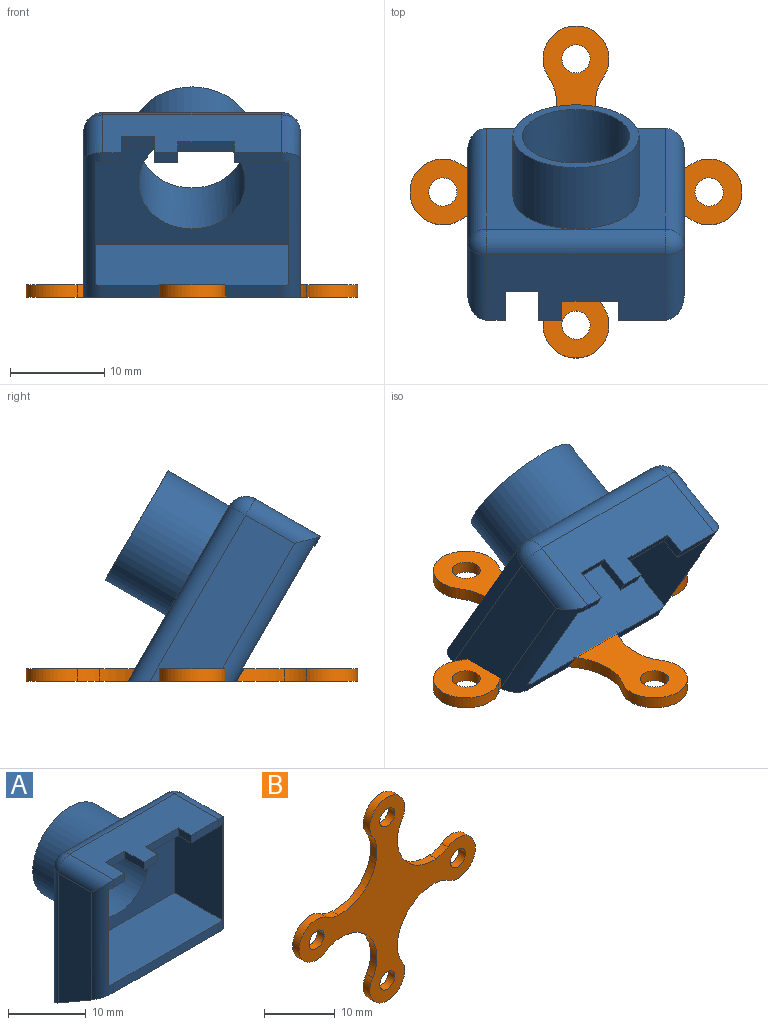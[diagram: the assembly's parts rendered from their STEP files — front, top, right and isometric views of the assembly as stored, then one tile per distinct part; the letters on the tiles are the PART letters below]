
ASSEMBLY  parts=2 mates=1
PART A: 32 faces, bbox 23x17.5x23.5 mm
  f0: plane 19x1.43mm, normal (0,-1,0), area 27.1mm2, adj f9,f22,f23,f29
  f1: plane 2x1.2mm, normal (0,-1,0), area 2.4mm2, adj f5,f6,f16,f23
  f2: plane 5x1.2mm, normal (0,-1,0), area 6mm2, adj f5,f6,f19,f29
  f3: plane 20.35x6mm, normal (1,0,0), area 111.7mm2, adj f22,f28,f29,f31
  f4: plane 2.5x1.2mm, normal (0,-1,0), area 3mm2, adj f5,f6,f17,f21
  f5: plane 19x8mm, normal (0,0,1), area 126mm2, adj f1,f2,f4,f16,f17,f18,f19,f20
  f6: plane 20.6x8.8mm, normal (0,0,-1), area 155.1mm2, adj f1,f2,f4,f10,f11,f12,f16,f17
  f7: plane 20.35x6mm, normal (-1,0,0), area 111.7mm2, adj f22,f23,f24,f25
  f8: plane 21.5x19mm, normal (0,1,0), area 267.5mm2, adj f14,f22,f25,f27,f28
  f9: plane 20.6x8.8mm, normal (0,0,1), area 181.2mm2, adj f0,f10,f11,f12,f23,f29
  f10: plane 15.1x8.63mm, normal (-1,0,0), area 130.4mm2, adj f6,f9,f12,f29
  f11: plane 15.1x8.63mm, normal (1,0,0), area 130.4mm2, adj f6,f9,f12,f23
  f12: plane 20.6x15.1mm, normal (0,-1,0), area 209mm2, adj f6,f9,f10,f11,f13
  f13: cylinder r=5.7mm len=11.4mm, axis (0,1,0), area 311.6mm2, adj f12,f15
  f14: cylinder r=6.7mm len=13.4mm, axis (0,-1,0), area 315.7mm2, adj f8,f15
  f15: plane 13.4x13.4mm, normal (0,1,0), area 39mm2, adj f13,f14
  f16: plane 3.5x1.2mm, normal (1,0,0), area 4.2mm2, adj f1,f5,f6,f18
  f17: plane 3.5x1.2mm, normal (-1,0,0), area 4.2mm2, adj f4,f5,f6,f18
  f18: plane 3.5x1.2mm, normal (0,-1,0), area 4.2mm2, adj f5,f6,f16,f17
  f19: plane 2.3x1.2mm, normal (-1,0,0), area 2.8mm2, adj f2,f5,f6,f20
  f20: plane 6x1.2mm, normal (0,-1,0), area 7.2mm2, adj f5,f6,f19,f21
  f21: plane 2.3x1.2mm, normal (1,0,0), area 2.8mm2, adj f4,f5,f6,f20
  f22: plane 23x10mm, normal (0,-0.5,-0.87), area 261.6mm2, adj f0,f3,f7,f8,f23,f25,f28,f29
  f23: cylinder r=2mm len=18.88mm, axis (0,0,1), area 42.3mm2, adj f0,f1,f6,f7,f9,f11,f22,f24
  f24: cylinder r=2mm len=8mm, axis (0,-1,0), area 22.8mm2, adj f5,f7,f23,f26
  f25: cylinder r=2mm len=21.5mm, axis (0,0,-1), area 66.2mm2, adj f7,f8,f22,f26
  f26: sphere r=2mm, area 6.3mm2, adj f24,f25,f27
  f27: cylinder r=2mm len=19mm, axis (-1,0,0), area 59.7mm2, adj f5,f8,f26,f30
  f28: cylinder r=2mm len=21.5mm, axis (0,0,1), area 66.2mm2, adj f3,f8,f22,f30
  f29: cylinder r=2mm len=18.88mm, axis (0,0,-1), area 42.3mm2, adj f0,f2,f3,f6,f9,f10,f22,f31
  f30: sphere r=2mm, area 6.3mm2, adj f27,f28,f31
  f31: cylinder r=2mm len=8mm, axis (0,1,0), area 22.8mm2, adj f3,f5,f29,f30
PART B: 22 faces, bbox 35.3x1.3x35.3 mm
  f0: cylinder r=5mm len=2.39mm, axis (0,1,0), area 3.3mm2, adj f1,f19,f20,f21
  f1: cylinder r=3.5mm len=7mm, axis (0,1,0), area 19.7mm2, adj f0,f2,f20,f21
  f2: cylinder r=5mm len=2.39mm, axis (0,1,0), area 3.3mm2, adj f1,f3,f20,f21
  f3: cylinder r=7.18mm len=7.75mm, axis (0,1,0), area 16.1mm2, adj f2,f4,f20,f21
  f4: cylinder r=5mm len=2.39mm, axis (0,1,0), area 3.3mm2, adj f3,f5,f20,f21
  f5: cylinder r=3.5mm len=7mm, axis (0,1,0), area 19.7mm2, adj f4,f6,f20,f21
  f6: cylinder r=5mm len=2.39mm, axis (0,1,0), area 3.3mm2, adj f5,f7,f20,f21
  f7: cylinder r=7.18mm len=7.75mm, axis (0,1,0), area 16.1mm2, adj f6,f8,f20,f21
  f8: cylinder r=5mm len=2.39mm, axis (0,1,0), area 3.3mm2, adj f7,f9,f20,f21
  f9: cylinder r=3.5mm len=7mm, axis (0,1,0), area 19.7mm2, adj f8,f10,f20,f21
  f10: cylinder r=5mm len=2.39mm, axis (0,1,0), area 3.3mm2, adj f9,f11,f20,f21
  f11: cylinder r=7.18mm len=7.75mm, axis (0,1,0), area 16.1mm2, adj f10,f12,f20,f21
  f12: cylinder r=5mm len=2.39mm, axis (0,1,0), area 3.3mm2, adj f11,f13,f20,f21
  f13: cylinder r=3.5mm len=7mm, axis (0,1,0), area 19.7mm2, adj f12,f14,f20,f21
  f14: cylinder r=5mm len=2.39mm, axis (0,1,0), area 3.3mm2, adj f13,f19,f20,f21
  f15: cylinder r=1.5mm len=3mm, axis (0,1,0), area 12.3mm2, adj f20,f21
  f16: cylinder r=1.5mm len=3mm, axis (0,1,0), area 12.3mm2, adj f20,f21
  f17: cylinder r=1.5mm len=3mm, axis (0,1,0), area 12.3mm2, adj f20,f21
  f18: cylinder r=1.5mm len=3mm, axis (0,1,0), area 12.3mm2, adj f20,f21
  f19: cylinder r=7.18mm len=7.75mm, axis (0,1,0), area 16.1mm2, adj f0,f14,f20,f21
  f20: plane 35.28x35.28mm, normal (0,-1,0), area 333.8mm2, adj f0,f1,f2,f3,f4,f5,f6,f7
  f21: plane 35.28x35.28mm, normal (0,1,0), area 333.8mm2, adj f0,f1,f2,f3,f4,f5,f6,f7
PLACE A rot(axis=(1,0,0),30deg) t=(-12.55,-97.01,6.98)mm
PLACE B rot(axis=(1,0,0),90deg) t=(-12.55,-96.41,-4.5)mm
MATE fastened A.f22 <-> B.f20  axis (0,0,-1) through (-12.55,-95.41,-5.8)mm
